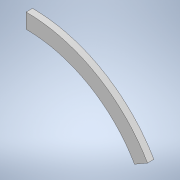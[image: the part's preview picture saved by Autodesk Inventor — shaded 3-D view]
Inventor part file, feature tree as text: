
AUTODESK INVENTOR PART (.ipt)
format: ipt  version: 2021.1 (Build 251245010, 245A)  size: 100,352 bytes
history: native  units: in
note: dims shown in document units (in); Inventor stores cm internally (conversion verified against a paired STEP export)
features: extrude x1, sketch x1
ambient origin geometry x8: Origin, YZ Plane, XZ Plane, XY Plane, X Axis, Y Axis, Z Axis, Center Point
bodies: Solid1 (feature_tree)
feature tree (2):
  extrude  "Extrusion1"  Depth=1.0in
  sketch  "Sketch1"  dims[d0=40.0in d1=0.35in d2=2.0in d3=60.0deg d4=1.0in d5=0.0in]
